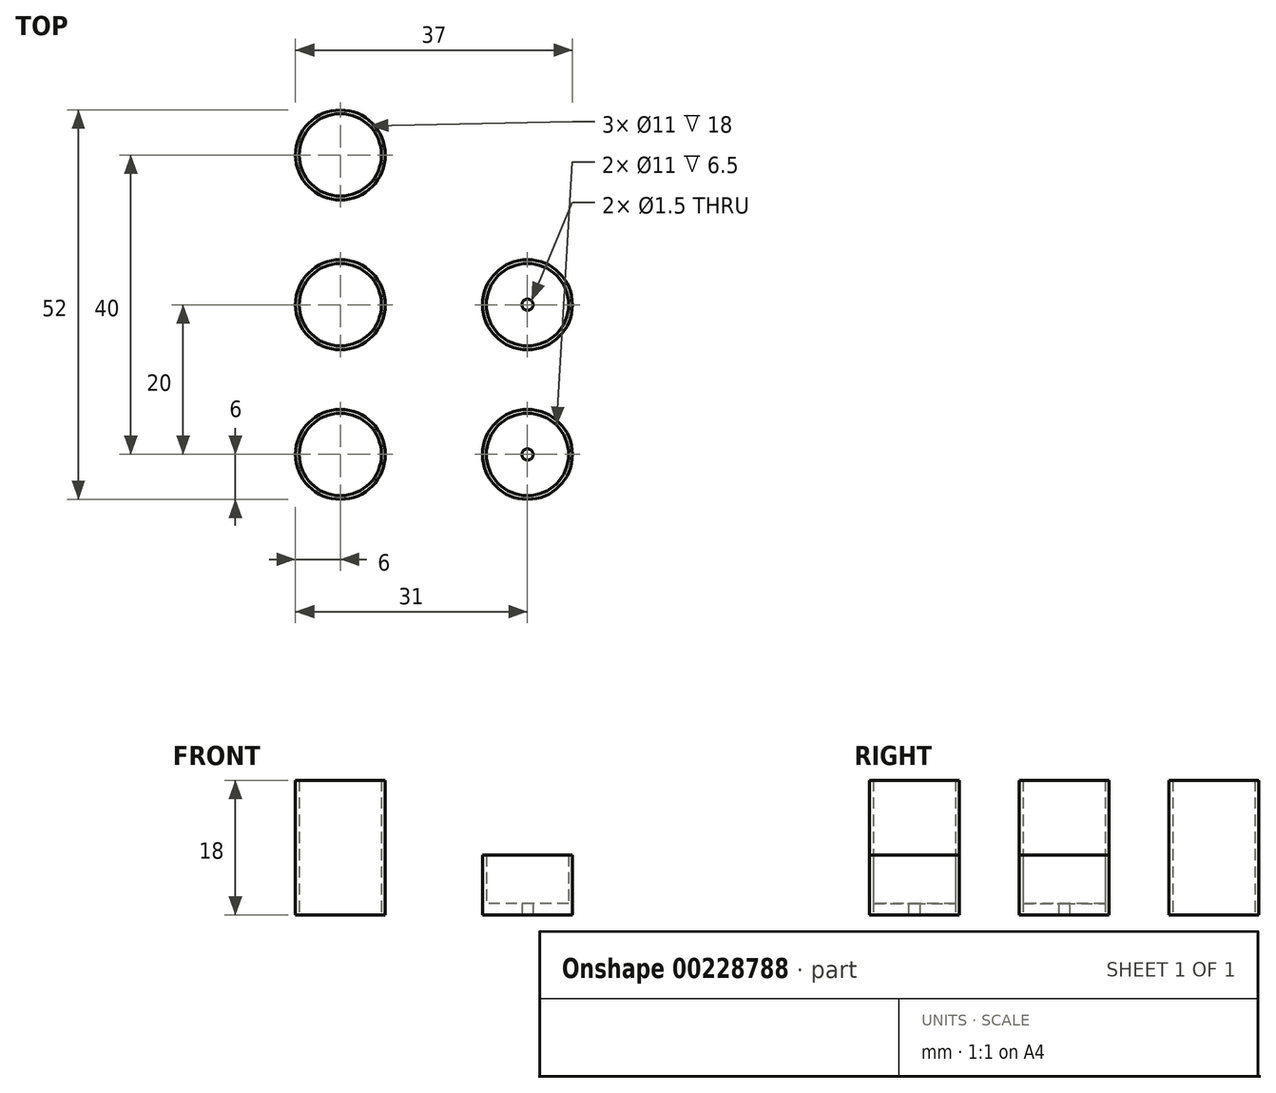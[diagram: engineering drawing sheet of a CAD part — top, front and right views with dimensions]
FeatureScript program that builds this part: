
annotation { "Feature Type Name" : "Feature", "Feature Type Description" : "" }
export const myFeature = defineFeature(function(context is Context, id is Id, definition is map)
    precondition{}
    {
        {
            var Q0;
            Q0=qCreatedBy(makeId("Top.planeOp"),FACE);
            var sketch = newSketch(context, id + "F0", { "sketchPlane" : qUnion([Q0])});
            skCircle(sketch, "E0", {"center": v(0, 0) * mm, "radius": 6 * mm});
            skCircle(sketch, "E1", {"center": v(0, 0) * mm, "radius": 5.5 * mm});
            skCircle(sketch, "E2", {"center": v(0, 0) * mm, "radius": 1.9 * mm});
            skCircle(sketch, "E3", {"center": v(0, 0) * mm, "radius": 2.4 * mm});
            skCircle(sketch, "E4", {"center": v(0, 0) * mm, "radius": 0.75 * mm});
            skCircle(sketch, "E5.MirrorC", {"center": v(-18, 0) * mm, "radius": 0.5 * mm});
            skCircle(sketch, "E6.1.0.0", {"center": v(25, 0) * mm, "radius": 5.5 * mm});
            skCircle(sketch, "E6.1.0.1", {"center": v(25, 0) * mm, "radius": 2.4 * mm});
            skCircle(sketch, "E6.1.0.2", {"center": v(25, 0) * mm, "radius": 6 * mm});
            skCircle(sketch, "E6.1.0.3", {"center": v(25, 0) * mm, "radius": 1.9 * mm});
            skCircle(sketch, "E6.1.0.4", {"center": v(25, 0) * mm, "radius": 0.75 * mm});
            skLineSegment(sketch, "E6.direction1", {"start": v(0, 0) * mm, "end": v(25, 0) * mm, "construction": true});
            skCircle(sketch, "E7.0.1.0", {"center": v(0, 20) * mm, "radius": 2.4 * mm});
            skCircle(sketch, "E7.0.1.1", {"center": v(0, 20) * mm, "radius": 5.5 * mm});
            skCircle(sketch, "E7.0.1.2", {"center": v(0, 20) * mm, "radius": 1.9 * mm});
            skCircle(sketch, "E7.0.1.3", {"center": v(0, 20) * mm, "radius": 0.75 * mm});
            skCircle(sketch, "E7.0.1.4", {"center": v(0, 20) * mm, "radius": 6 * mm});
            skCircle(sketch, "E7.0.2.0", {"center": v(0, 40) * mm, "radius": 2.4 * mm});
            skCircle(sketch, "E7.0.2.1", {"center": v(0, 40) * mm, "radius": 5.5 * mm});
            skCircle(sketch, "E7.0.2.2", {"center": v(0, 40) * mm, "radius": 1.9 * mm});
            skCircle(sketch, "E7.0.2.3", {"center": v(0, 40) * mm, "radius": 0.75 * mm});
            skCircle(sketch, "E7.0.2.4", {"center": v(0, 40) * mm, "radius": 6 * mm});
            skLineSegment(sketch, "E7.direction2", {"start": v(0, 0) * mm, "end": v(0, 20) * mm, "construction": true});
            skCircle(sketch, "E8.0.1.0", {"center": v(25, 20) * mm, "radius": 2.4 * mm});
            skCircle(sketch, "E8.0.1.1", {"center": v(25, 20) * mm, "radius": 1.9 * mm});
            skCircle(sketch, "E8.0.1.2", {"center": v(25, 20) * mm, "radius": 5.5 * mm});
            skCircle(sketch, "E8.0.1.3", {"center": v(25, 20) * mm, "radius": 6 * mm});
            skCircle(sketch, "E8.0.1.4", {"center": v(25, 20) * mm, "radius": 0.75 * mm});
            skLineSegment(sketch, "E8.direction1", {"start": v(25, 0) * mm, "end": v(50, 0) * mm, "construction": true});
            skLineSegment(sketch, "E8.direction2", {"start": v(25, 0) * mm, "end": v(25, 20) * mm, "construction": true});
            skSolve(sketch);
        }
        {
            var Q0;
            Q0=makeQuery(id+"F0.imprint","IMPRINT",FACE,{"disambiguationData":[TD([[makeQuery(id+"F0.imprint","IMPRINT",EDGE,{"derivedFrom":sQuery(id+"F0.wireOp",EDGE,"E0")}),1.0]])]});
            var Q1;
            Q1=makeQuery(id+"F0.imprint","IMPRINT",FACE,{"disambiguationData":[TD([[makeQuery(id+"F0.imprint","IMPRINT",EDGE,{"derivedFrom":sQuery(id+"F0.wireOp",EDGE,"E7.0.1.1")}),-1.0]])]});
            var Q2;
            Q2=makeQuery(id+"F0.imprint","IMPRINT",FACE,{"disambiguationData":[TD([[makeQuery(id+"F0.imprint","IMPRINT",EDGE,{"derivedFrom":sQuery(id+"F0.wireOp",EDGE,"E7.0.2.1")}),-1.0]])]});
            extrude(context, id + "F1", {"entities" : qUnion([Q0, Q1, Q2]), "depth" : 18 * mm});
        }
        {
            var Q0;
            Q0=makeQuery(id+"F0.imprint","IMPRINT",FACE,{"disambiguationData":[TD([[makeQuery(id+"F0.imprint","IMPRINT",EDGE,{"derivedFrom":sQuery(id+"F0.wireOp",EDGE,"E6.1.0.0")}),-1.0]])]});
            var Q1;
            Q1=makeQuery(id+"F0.imprint","IMPRINT",FACE,{"disambiguationData":[TD([[makeQuery(id+"F0.imprint","IMPRINT",EDGE,{"derivedFrom":sQuery(id+"F0.wireOp",EDGE,"E8.0.1.2")}),-1.0]])]});
            extrude(context, id + "F2", {"entities" : qUnion([Q0, Q1]), "depth" : 8 * mm});
        }
        {
            var Q0;
            Q0=makeQuery(id+"F0.imprint","IMPRINT",FACE,{"disambiguationData":[TD([[makeQuery(id+"F0.imprint","IMPRINT",EDGE,{"derivedFrom":sQuery(id+"F0.wireOp",EDGE,"E6.1.0.0")}),1.0]])]});
            var Q1;
            Q1=makeQuery(id+"F0.imprint","IMPRINT",FACE,{"disambiguationData":[TD([[makeQuery(id+"F0.imprint","IMPRINT",EDGE,{"derivedFrom":sQuery(id+"F0.wireOp",EDGE,"E6.1.0.1")}),1.0]])]});
            var Q2;
            Q2=makeQuery(id+"F0.imprint","IMPRINT",FACE,{"disambiguationData":[TD([[makeQuery(id+"F0.imprint","IMPRINT",EDGE,{"derivedFrom":sQuery(id+"F0.wireOp",EDGE,"E6.1.0.3")}),1.0]])]});
            var Q3;
            Q3=makeQuery(id+"F0.imprint","IMPRINT",FACE,{"disambiguationData":[TD([[makeQuery(id+"F0.imprint","IMPRINT",EDGE,{"derivedFrom":sQuery(id+"F0.wireOp",EDGE,"E8.0.1.0")}),-1.0]])]});
            var Q4;
            Q4=makeQuery(id+"F0.imprint","IMPRINT",FACE,{"disambiguationData":[TD([[makeQuery(id+"F0.imprint","IMPRINT",EDGE,{"derivedFrom":sQuery(id+"F0.wireOp",EDGE,"E8.0.1.0")}),1.0]])]});
            var Q5;
            Q5=makeQuery(id+"F0.imprint","IMPRINT",FACE,{"disambiguationData":[TD([[makeQuery(id+"F0.imprint","IMPRINT",EDGE,{"derivedFrom":sQuery(id+"F0.wireOp",EDGE,"E8.0.1.1")}),1.0]])]});
            extrude(context, id + "F3", {"entities" : qUnion([Q0, Q1, Q2, Q3, Q4, Q5]), "operationType" : NewBodyOperationType.ADD, "depth" : 1.5 * mm});
        }
    });
